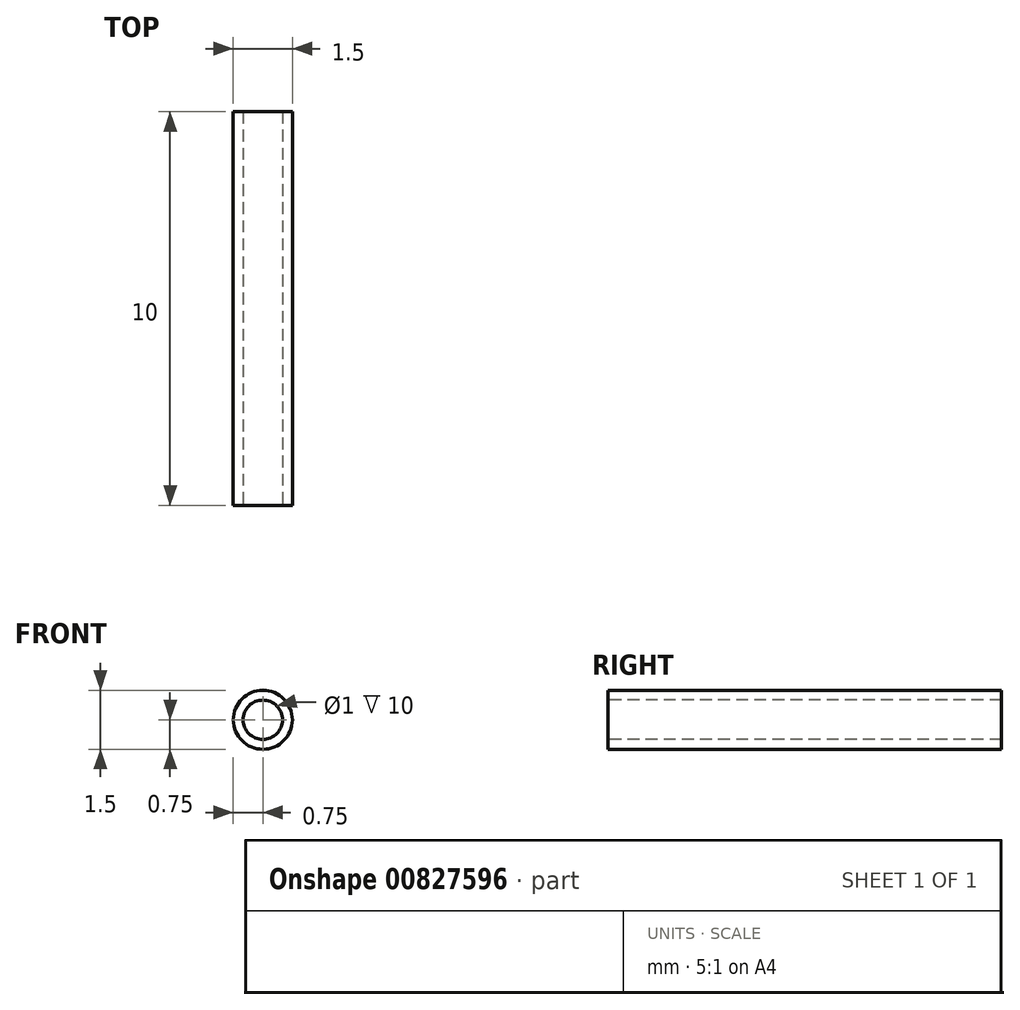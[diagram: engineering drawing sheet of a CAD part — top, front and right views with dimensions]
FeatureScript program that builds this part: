
annotation { "Feature Type Name" : "Feature", "Feature Type Description" : "" }
export const myFeature = defineFeature(function(context is Context, id is Id, definition is map)
    precondition{}
    {
        {
            var Q0;
            Q0=qCreatedBy(makeId("Front.planeOp"),FACE);
            var sketch = newSketch(context, id + "F0", { "sketchPlane" : qUnion([Q0])});
            skCircle(sketch, "E0", {"center": v(0, 0) * mm, "radius": 0.75 * mm});
            skSolve(sketch);
        }
        {
            var Q0;
            Q0=qSketchRegion(id+"F0",true);
            extrude(context, id + "F1", {"entities" : qUnion([Q0]), "depth" : 10 * mm});
        }
        {
            var Q0;
            Q0=makeQuery(id+"F1.opExtrude","CAP_FACE",FACE,{"disambiguationData":[OSD([sQuery(id+"F0.wireOp",EDGE,"E0")])],"isStart":false});
            var sketch = newSketch(context, id + "F2", { "sketchPlane" : qUnion([Q0])});
            skCircle(sketch, "E1", {"center": v(0, 0) * mm, "radius": 0.5 * mm});
            skSolve(sketch);
        }
        {
            var Q0;
            Q0=qSketchRegion(id+"F2",true);
            extrude(context, id + "F3", {"entities" : qUnion([Q0]), "operationType" : NewBodyOperationType.REMOVE, "endBound" : BoundingType.THROUGH_ALL, "oppositeDirection" : true, "depth" : 25 * mm});
        }
    });
